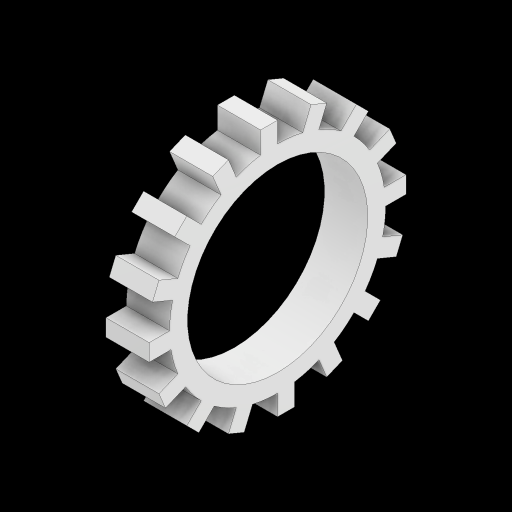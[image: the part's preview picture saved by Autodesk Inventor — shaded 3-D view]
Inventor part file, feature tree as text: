
AUTODESK INVENTOR PART (.ipt)
format: ipt  version: 2023 (Build 270158000, 158)  size: 201,216 bytes
history: native  units: mm
features: sketch x1, extrude x1
ambient origin geometry x8: Origin, YZ Plane, XZ Plane, XY Plane, X Axis, Y Axis, Z Axis, Center Point
bodies: Solid1 (feature_tree)
feature tree (2):
  sketch  "Sketch1"  dims[d0=26.5mm d1=31.75mm d3=3.0mm d4=2.5mm d5=160.0mm d7=360.0deg d9=6.35mm d10=0.0mm]
  extrude  "Extrusion1"  Depth=6.35mm
